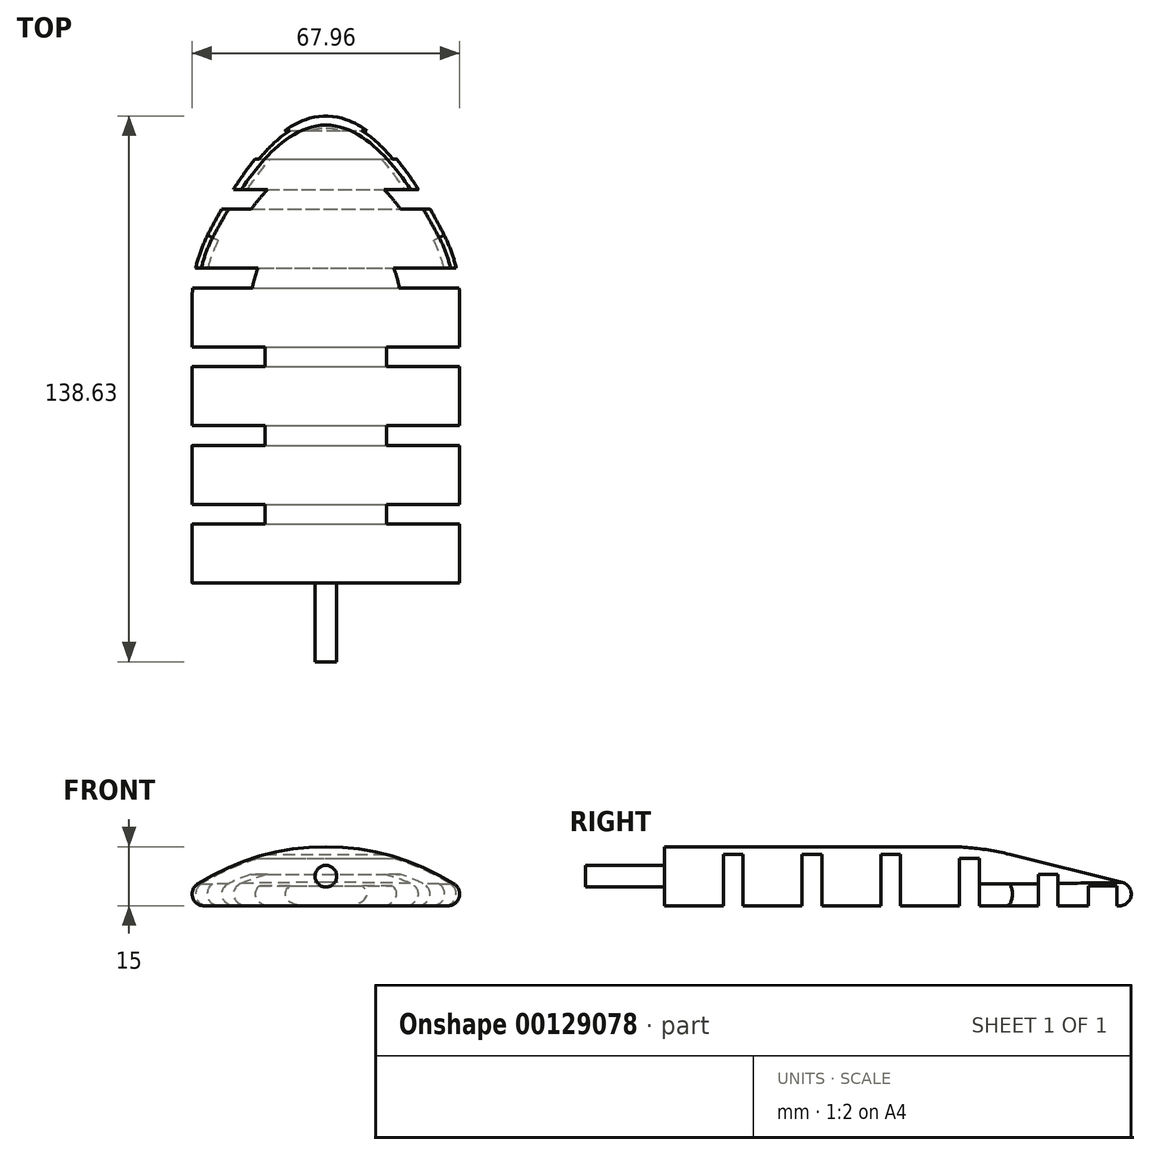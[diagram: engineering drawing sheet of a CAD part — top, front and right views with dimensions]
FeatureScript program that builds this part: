
annotation { "Feature Type Name" : "Feature", "Feature Type Description" : "" }
export const myFeature = defineFeature(function(context is Context, id is Id, definition is map)
    precondition{}
    {
        {
            var Q0;
            Q0=qCreatedBy(makeId("Front.planeOp"),FACE);
            var sketch = newSketch(context, id + "F0", { "sketchPlane" : qUnion([Q0])});
            skLineSegment(sketch, "E0", {"start": v(0, 0) * mm, "end": v(-40, 0) * mm});
            skLineSegment(sketch, "E1", {"start": v(0, 0) * mm, "end": v(40, 0) * mm});
            skArc(sketch, "E2", {"start": v(40, 0) * mm, "mid": v(0, 15) * mm, "end": v(-40, 0) * mm});
            skSolve(sketch);
        }
        {
            var Q0;
            Q0=makeQuery(id+"F0.imprint","IMPRINT",FACE,{"disambiguationData":[TD([[makeQuery(id+"F0.imprint","IMPRINT",EDGE,{"derivedFrom":sQuery(id+"F0.wireOp",EDGE,"E0")}),-1.0]])]});
            extrude(context, id + "F1", {"entities" : qUnion([Q0]), "endBound" : BoundingType.SYMMETRIC, "depth" : 100 * mm});
        }
        {
            var Q0;
            Q0=makeQuery(id+"F1.opExtrude","CAP_EDGE",EDGE,{"disambiguationData":[OSD([sQuery(id+"F0.wireOp",EDGE,"E2")])],"isStart":true});
            chamfer(context, id + "F2", {"entities" : qUnion([Q0]), "chamferType" : ChamferType.TWO_OFFSETS, "width1" : 60 * mm, "oppositeDirection" : false, "width2" : 15 * mm, "tangentPropagation" : true});
        }
        {
            var Q0;
            Q0=makeQuery(id+"F2.opChamfer","BLEND_EDGE",EDGE,{"disambiguationData":[OD(0.0)],"blendedFrom":[makeQuery(id+"F1.opExtrude","CAP_EDGE",EDGE,{"disambiguationData":[OSD([sQuery(id+"F0.wireOp",EDGE,"E2")])],"isStart":true}),makeQuery(id+"F1.opExtrude","SWEPT_FACE",FACE,{"disambiguationData":[OSD([sQuery(id+"F0.wireOp",EDGE,"E0"),sQuery(id+"F0.wireOp",EDGE,"E1")])]})],"blendedInto":[makeQuery(id+"F1.opExtrude","SWEPT_FACE",FACE,{"disambiguationData":[OSD([sQuery(id+"F0.wireOp",EDGE,"E0"),sQuery(id+"F0.wireOp",EDGE,"E1")])]})]});
            var Q1;
            Q1=makeQuery(id+"F2.opChamfer","BLEND_EDGE",EDGE,{"disambiguationData":[OD(1.0)],"blendedFrom":[makeQuery(id+"F1.opExtrude","CAP_EDGE",EDGE,{"disambiguationData":[OSD([sQuery(id+"F0.wireOp",EDGE,"E2")])],"isStart":true}),makeQuery(id+"F1.opExtrude","SWEPT_FACE",FACE,{"disambiguationData":[OSD([sQuery(id+"F0.wireOp",EDGE,"E0"),sQuery(id+"F0.wireOp",EDGE,"E1")])]})],"blendedInto":[makeQuery(id+"F1.opExtrude","SWEPT_FACE",FACE,{"disambiguationData":[OSD([sQuery(id+"F0.wireOp",EDGE,"E0"),sQuery(id+"F0.wireOp",EDGE,"E1")])]})]});
            var Q2;
            Q2=makeQuery(id+"F1.opExtrude","SWEPT_EDGE",EDGE,{"disambiguationData":[OSD([sQuery(id+"F0.wireOp",EDGE,"E0"),sQuery(id+"F0.wireOp",EDGE,"E2")])]});
            var Q3;
            Q3=makeQuery(id+"F1.opExtrude","SWEPT_EDGE",EDGE,{"disambiguationData":[OSD([sQuery(id+"F0.wireOp",EDGE,"E1"),sQuery(id+"F0.wireOp",EDGE,"E2")])]});
            fillet(context, id + "F3", {"entities" : qUnion([Q0, Q1, Q2, Q3]), "radius" : 3 * mm, "tangentPropagation" : true, "allowEdgeOverflow" : false});
        }
        {
            var Q0;
            Q0=makeQuery(id+"F1.opExtrude","CAP_FACE",FACE,{"disambiguationData":[OSD([sQuery(id+"F0.wireOp",EDGE,"E0"),sQuery(id+"F0.wireOp",EDGE,"E1"),sQuery(id+"F0.wireOp",EDGE,"E2")])],"isStart":false});
            extrude(context, id + "F4", {"entities" : qUnion([Q0]), "operationType" : NewBodyOperationType.ADD, "depth" : 40 * mm});
        }
        {
            var Q0;
            {var subQ0=sQuery(id+"F0.wireOp",EDGE,"E0");var subQ1=sQuery(id+"F0.wireOp",EDGE,"E2");Q0=makeQuery(id+"F3.opFillet","BLEND_EDGE",EDGE,{"blendedFrom":[makeQuery(id+"F1.opExtrude","SWEPT_EDGE",EDGE,{"disambiguationData":[OSD([subQ0,subQ1])]}),makeQuery(id+"F2.opChamfer","BLEND_EDGE",EDGE,{"disambiguationData":[OD(0.0)],"blendedFrom":[makeQuery(id+"F1.opExtrude","CAP_EDGE",EDGE,{"disambiguationData":[OSD([subQ1])],"isStart":true}),makeQuery(id+"F1.opExtrude","SWEPT_FACE",FACE,{"disambiguationData":[OSD([subQ0,sQuery(id+"F0.wireOp",EDGE,"E1")])]})],"blendedInto":[makeQuery(id+"F1.opExtrude","SWEPT_FACE",FACE,{"disambiguationData":[OSD([subQ0,sQuery(id+"F0.wireOp",EDGE,"E1")])]})]})],"blendedInto":[]});}
            fillet(context, id + "F5", {"entities" : qUnion([Q0]), "radius" : 65 * mm, "tangentPropagation" : true, "allowEdgeOverflow" : false});
        }
        {
            var Q0;
            Q0=makeQuery(id+"F4.opExtrude","CAP_FACE",FACE,{"disambiguationData":[OSD([sQuery(id+"F0.wireOp",EDGE,"E0"),sQuery(id+"F0.wireOp",EDGE,"E1"),sQuery(id+"F0.wireOp",EDGE,"E2")])],"isStart":false});
            var sketch = newSketch(context, id + "F6", { "sketchPlane" : qUnion([Q0])});
            skLineSegment(sketch, "E3", {"start": v(0, 0) * mm, "end": v(0, 15) * mm});
            skLineSegment(sketch, "E4", {"start": v(0, 7.5) * mm, "end": v(13.56, 7.5) * mm});
            skPoint(sketch, "E4.endSnap0", {"position": v(0, 7.5) * mm});
            skLineSegment(sketch, "E5", {"start": v(0, 7.5) * mm, "end": v(-13.5, 7.5) * mm});
            skCircle(sketch, "E6", {"center": v(0, 7.5) * mm, "radius": 2.75 * mm});
            skSolve(sketch);
        }
        {
            var Q0;
            {var subQ0=sQuery(id+"F6.wireOp",EDGE,"E4");var subQ3=sQuery(id+"F6.wireOp",EDGE,"E6");var subQ5=makeQuery(id+"F6.imprint","INTERSECT",VERTEX,{"derivedFrom":[subQ0,subQ3]});Q0=makeQuery(id+"F6.imprint","IMPRINT",FACE,{"disambiguationData":[TD([[makeQuery(id+"F6.imprint","IMPRINT",EDGE,{"disambiguationData":[TD([[subQ5,-1.0]])],"derivedFrom":subQ3}),1.0]])]});}
            var Q1;
            {var subQ0=sQuery(id+"F6.wireOp",EDGE,"E4");var subQ3=sQuery(id+"F6.wireOp",EDGE,"E6");var subQ5=makeQuery(id+"F6.imprint","INTERSECT",VERTEX,{"derivedFrom":[subQ0,subQ3]});Q1=makeQuery(id+"F6.imprint","IMPRINT",FACE,{"disambiguationData":[TD([[makeQuery(id+"F6.imprint","IMPRINT",EDGE,{"disambiguationData":[TD([[subQ5,1.0]])],"derivedFrom":subQ3}),1.0]])]});}
            var Q2;
            {var subQ0=sQuery(id+"F6.wireOp",EDGE,"E5");var subQ3=sQuery(id+"F6.wireOp",EDGE,"E6");var subQ5=makeQuery(id+"F6.imprint","INTERSECT",VERTEX,{"derivedFrom":[subQ0,subQ3]});Q2=makeQuery(id+"F6.imprint","IMPRINT",FACE,{"disambiguationData":[TD([[makeQuery(id+"F6.imprint","IMPRINT",EDGE,{"disambiguationData":[TD([[subQ5,-1.0]])],"derivedFrom":subQ3}),1.0]])]});}
            var Q3;
            {var subQ0=sQuery(id+"F6.wireOp",EDGE,"E5");var subQ3=sQuery(id+"F6.wireOp",EDGE,"E6");var subQ5=makeQuery(id+"F6.imprint","INTERSECT",VERTEX,{"derivedFrom":[subQ0,subQ3]});Q3=makeQuery(id+"F6.imprint","IMPRINT",FACE,{"disambiguationData":[TD([[makeQuery(id+"F6.imprint","IMPRINT",EDGE,{"disambiguationData":[TD([[subQ5,1.0]])],"derivedFrom":subQ3}),1.0]])]});}
            extrude(context, id + "F7", {"entities" : qUnion([Q0, Q1, Q2, Q3]), "operationType" : NewBodyOperationType.ADD, "depth" : 20 * mm});
        }
        {
            var Q0;
            {var subQ0=sQuery(id+"F0.wireOp",EDGE,"E1");var subQ1=sQuery(id+"F0.wireOp",EDGE,"E0");Q0=makeQuery(id+"F4.boolean.opBoolean","MERGE",FACE,{"derivedFrom":[makeQuery(id+"F1.opExtrude","SWEPT_FACE",FACE,{"disambiguationData":[OSD([subQ1,subQ0])]}),makeQuery(id+"F4.opExtrude","SWEPT_FACE",FACE,{"disambiguationData":[OSD([subQ1,subQ0])]})]});}
            var sketch = newSketch(context, id + "F8", { "sketchPlane" : qUnion([Q0])});
            skLineSegment(sketch, "E7", {"start": v(0, 90) * mm, "end": v(0, -25.63) * mm});
            skPoint(sketch, "E8", {"position": v(0, 75) * mm});
            skPoint(sketch, "E9", {"position": v(0, 70) * mm});
            skPoint(sketch, "E10", {"position": v(0, 55) * mm});
            skPoint(sketch, "E11", {"position": v(0, 50) * mm});
            skPoint(sketch, "E12", {"position": v(0, 35) * mm});
            skPoint(sketch, "E13", {"position": v(0, 30) * mm});
            skPoint(sketch, "E14", {"position": v(0, 15) * mm});
            skPoint(sketch, "E15", {"position": v(0, 10) * mm});
            skPoint(sketch, "E16", {"position": v(0, -5) * mm});
            skPoint(sketch, "E17", {"position": v(0, -10) * mm});
            skPoint(sketch, "E18", {"position": v(0, -25) * mm});
            skLineSegment(sketch, "E19", {"start": v(0, 70) * mm, "end": v(-30.98, 70) * mm});
            skLineSegment(sketch, "E20", {"start": v(0, 75) * mm, "end": v(30.98, 75) * mm});
            skLineSegment(sketch, "E21.bottom", {"start": v(-46.57, 70) * mm, "end": v(50.6, 70) * mm});
            skLineSegment(sketch, "E21.top", {"start": v(-46.57, 75) * mm, "end": v(50.6, 75) * mm});
            skLineSegment(sketch, "E21.left", {"start": v(-46.57, 70) * mm, "end": v(-46.57, 75) * mm});
            skLineSegment(sketch, "E21.right", {"start": v(50.6, 70) * mm, "end": v(50.6, 75) * mm});
            skLineSegment(sketch, "E22.bottom", {"start": v(-46.86, 50) * mm, "end": v(50.6, 50) * mm});
            skLineSegment(sketch, "E22.top", {"start": v(-46.86, 55) * mm, "end": v(50.6, 55) * mm});
            skLineSegment(sketch, "E22.left", {"start": v(-46.86, 50) * mm, "end": v(-46.86, 55) * mm});
            skLineSegment(sketch, "E22.right", {"start": v(50.6, 50) * mm, "end": v(50.6, 55) * mm});
            skLineSegment(sketch, "E23.bottom", {"start": v(-45.7, 30) * mm, "end": v(42.8, 30) * mm});
            skLineSegment(sketch, "E23.top", {"start": v(-45.7, 35) * mm, "end": v(42.8, 35) * mm});
            skLineSegment(sketch, "E23.left", {"start": v(-45.7, 30) * mm, "end": v(-45.7, 35) * mm});
            skLineSegment(sketch, "E23.right", {"start": v(42.8, 30) * mm, "end": v(42.8, 35) * mm});
            skLineSegment(sketch, "E24.bottom", {"start": v(-43.37, 15) * mm, "end": v(40.63, 15) * mm});
            skLineSegment(sketch, "E24.top", {"start": v(-43.37, 10) * mm, "end": v(40.63, 10) * mm});
            skLineSegment(sketch, "E24.left", {"start": v(-43.37, 15) * mm, "end": v(-43.37, 10) * mm});
            skLineSegment(sketch, "E24.right", {"start": v(40.63, 15) * mm, "end": v(40.63, 10) * mm});
            skLineSegment(sketch, "E25.bottom", {"start": v(-43.56, -5) * mm, "end": v(47.17, -5) * mm});
            skLineSegment(sketch, "E25.top", {"start": v(-43.56, -10) * mm, "end": v(47.17, -10) * mm});
            skLineSegment(sketch, "E25.left", {"start": v(-43.56, -5) * mm, "end": v(-43.56, -10) * mm});
            skLineSegment(sketch, "E25.right", {"start": v(47.17, -5) * mm, "end": v(47.17, -10) * mm});
            skLineSegment(sketch, "E26.bottom", {"start": v(-30.89, -25) * mm, "end": v(32.7, -25) * mm});
            skLineSegment(sketch, "E26.top", {"start": v(-30.89, -17.74) * mm, "end": v(32.7, -17.74) * mm});
            skLineSegment(sketch, "E26.left", {"start": v(-30.89, -25) * mm, "end": v(-30.89, -17.74) * mm});
            skLineSegment(sketch, "E26.right", {"start": v(32.7, -25) * mm, "end": v(32.7, -17.74) * mm});
            skSolve(sketch);
        }
        {
            var Q0;
            {var subQ0=sQuery(id+"F8.wireOp",EDGE,"E26.left");Q0=makeQuery(id+"F8.imprint","IMPRINT",FACE,{"disambiguationData":[TD([[makeQuery(id+"F8.imprint","IMPRINT",EDGE,{"derivedFrom":subQ0}),-1.0]])]});}
            var Q1;
            {var subQ0=sQuery(id+"F8.wireOp",EDGE,"E26.top");var subQ1=sQuery(id+"F8.wireOp",EDGE,"E7");var subQ2=makeQuery(id+"F8.imprint","INTERSECT",VERTEX,{"derivedFrom":[subQ1,subQ0]});Q1=makeQuery(id+"F8.imprint","IMPRINT",FACE,{"disambiguationData":[TD([[makeQuery(id+"F8.imprint","IMPRINT",EDGE,{"disambiguationData":[TD([[subQ2,-1.0]])],"derivedFrom":subQ1}),-1.0]])]});}
            var Q2;
            {var subQ0=sQuery(id+"F8.wireOp",EDGE,"E26.top");var subQ1=sQuery(id+"F8.wireOp",EDGE,"E7");var subQ2=makeQuery(id+"F8.imprint","INTERSECT",VERTEX,{"derivedFrom":[subQ1,subQ0]});Q2=makeQuery(id+"F8.imprint","IMPRINT",FACE,{"disambiguationData":[TD([[makeQuery(id+"F8.imprint","IMPRINT",EDGE,{"disambiguationData":[TD([[subQ2,-1.0]])],"derivedFrom":subQ1}),1.0]])]});}
            var Q3;
            {var subQ0=sQuery(id+"F8.wireOp",EDGE,"E26.right");Q3=makeQuery(id+"F8.imprint","IMPRINT",FACE,{"disambiguationData":[TD([[makeQuery(id+"F8.imprint","IMPRINT",EDGE,{"derivedFrom":subQ0}),1.0]])]});}
            var Q4;
            {var subQ0=sQuery(id+"F8.wireOp",EDGE,"E25.right");Q4=makeQuery(id+"F8.imprint","IMPRINT",FACE,{"disambiguationData":[TD([[makeQuery(id+"F8.imprint","IMPRINT",EDGE,{"derivedFrom":subQ0}),-1.0]])]});}
            var Q5;
            {var subQ0=sQuery(id+"F8.wireOp",EDGE,"E25.bottom");var subQ1=sQuery(id+"F8.wireOp",EDGE,"E7");var subQ2=makeQuery(id+"F8.imprint","INTERSECT",VERTEX,{"derivedFrom":[subQ1,subQ0]});Q5=makeQuery(id+"F8.imprint","IMPRINT",FACE,{"disambiguationData":[TD([[makeQuery(id+"F8.imprint","IMPRINT",EDGE,{"disambiguationData":[TD([[subQ2,-1.0]])],"derivedFrom":subQ1}),1.0]])]});}
            var Q6;
            {var subQ0=sQuery(id+"F8.wireOp",EDGE,"E25.bottom");var subQ1=sQuery(id+"F8.wireOp",EDGE,"E7");var subQ2=makeQuery(id+"F8.imprint","INTERSECT",VERTEX,{"derivedFrom":[subQ1,subQ0]});Q6=makeQuery(id+"F8.imprint","IMPRINT",FACE,{"disambiguationData":[TD([[makeQuery(id+"F8.imprint","IMPRINT",EDGE,{"disambiguationData":[TD([[subQ2,-1.0]])],"derivedFrom":subQ1}),-1.0]])]});}
            var Q7;
            {var subQ0=sQuery(id+"F8.wireOp",EDGE,"E25.left");Q7=makeQuery(id+"F8.imprint","IMPRINT",FACE,{"disambiguationData":[TD([[makeQuery(id+"F8.imprint","IMPRINT",EDGE,{"derivedFrom":subQ0}),1.0]])]});}
            var Q8;
            {var subQ0=sQuery(id+"F8.wireOp",EDGE,"E24.left");Q8=makeQuery(id+"F8.imprint","IMPRINT",FACE,{"disambiguationData":[TD([[makeQuery(id+"F8.imprint","IMPRINT",EDGE,{"derivedFrom":subQ0}),1.0]])]});}
            var Q9;
            {var subQ0=sQuery(id+"F8.wireOp",EDGE,"E24.bottom");var subQ1=sQuery(id+"F8.wireOp",EDGE,"E7");var subQ2=makeQuery(id+"F8.imprint","INTERSECT",VERTEX,{"derivedFrom":[subQ1,subQ0]});Q9=makeQuery(id+"F8.imprint","IMPRINT",FACE,{"disambiguationData":[TD([[makeQuery(id+"F8.imprint","IMPRINT",EDGE,{"disambiguationData":[TD([[subQ2,-1.0]])],"derivedFrom":subQ1}),-1.0]])]});}
            var Q10;
            {var subQ0=sQuery(id+"F8.wireOp",EDGE,"E24.bottom");var subQ1=sQuery(id+"F8.wireOp",EDGE,"E7");var subQ2=makeQuery(id+"F8.imprint","INTERSECT",VERTEX,{"derivedFrom":[subQ1,subQ0]});Q10=makeQuery(id+"F8.imprint","IMPRINT",FACE,{"disambiguationData":[TD([[makeQuery(id+"F8.imprint","IMPRINT",EDGE,{"disambiguationData":[TD([[subQ2,-1.0]])],"derivedFrom":subQ1}),1.0]])]});}
            var Q11;
            {var subQ0=sQuery(id+"F8.wireOp",EDGE,"E24.right");Q11=makeQuery(id+"F8.imprint","IMPRINT",FACE,{"disambiguationData":[TD([[makeQuery(id+"F8.imprint","IMPRINT",EDGE,{"derivedFrom":subQ0}),-1.0]])]});}
            var Q12;
            {var subQ0=sQuery(id+"F8.wireOp",EDGE,"E23.right");Q12=makeQuery(id+"F8.imprint","IMPRINT",FACE,{"disambiguationData":[TD([[makeQuery(id+"F8.imprint","IMPRINT",EDGE,{"derivedFrom":subQ0}),1.0]])]});}
            var Q13;
            {var subQ0=sQuery(id+"F8.wireOp",EDGE,"E23.top");var subQ1=sQuery(id+"F8.wireOp",EDGE,"E7");var subQ2=makeQuery(id+"F8.imprint","INTERSECT",VERTEX,{"derivedFrom":[subQ1,subQ0]});Q13=makeQuery(id+"F8.imprint","IMPRINT",FACE,{"disambiguationData":[TD([[makeQuery(id+"F8.imprint","IMPRINT",EDGE,{"disambiguationData":[TD([[subQ2,-1.0]])],"derivedFrom":subQ1}),1.0]])]});}
            var Q14;
            {var subQ0=sQuery(id+"F8.wireOp",EDGE,"E23.top");var subQ1=sQuery(id+"F8.wireOp",EDGE,"E7");var subQ2=makeQuery(id+"F8.imprint","INTERSECT",VERTEX,{"derivedFrom":[subQ1,subQ0]});Q14=makeQuery(id+"F8.imprint","IMPRINT",FACE,{"disambiguationData":[TD([[makeQuery(id+"F8.imprint","IMPRINT",EDGE,{"disambiguationData":[TD([[subQ2,-1.0]])],"derivedFrom":subQ1}),-1.0]])]});}
            var Q15;
            {var subQ0=sQuery(id+"F8.wireOp",EDGE,"E23.left");Q15=makeQuery(id+"F8.imprint","IMPRINT",FACE,{"disambiguationData":[TD([[makeQuery(id+"F8.imprint","IMPRINT",EDGE,{"derivedFrom":subQ0}),-1.0]])]});}
            var Q16;
            {var subQ0=sQuery(id+"F8.wireOp",EDGE,"E22.left");Q16=makeQuery(id+"F8.imprint","IMPRINT",FACE,{"disambiguationData":[TD([[makeQuery(id+"F8.imprint","IMPRINT",EDGE,{"derivedFrom":subQ0}),-1.0]])]});}
            var Q17;
            {var subQ0=sQuery(id+"F8.wireOp",EDGE,"E22.top");var subQ1=sQuery(id+"F8.wireOp",EDGE,"E7");var subQ2=makeQuery(id+"F8.imprint","INTERSECT",VERTEX,{"derivedFrom":[subQ1,subQ0]});Q17=makeQuery(id+"F8.imprint","IMPRINT",FACE,{"disambiguationData":[TD([[makeQuery(id+"F8.imprint","IMPRINT",EDGE,{"disambiguationData":[TD([[subQ2,-1.0]])],"derivedFrom":subQ1}),-1.0]])]});}
            var Q18;
            {var subQ0=sQuery(id+"F8.wireOp",EDGE,"E22.top");var subQ1=sQuery(id+"F8.wireOp",EDGE,"E7");var subQ2=makeQuery(id+"F8.imprint","INTERSECT",VERTEX,{"derivedFrom":[subQ1,subQ0]});Q18=makeQuery(id+"F8.imprint","IMPRINT",FACE,{"disambiguationData":[TD([[makeQuery(id+"F8.imprint","IMPRINT",EDGE,{"disambiguationData":[TD([[subQ2,-1.0]])],"derivedFrom":subQ1}),1.0]])]});}
            var Q19;
            {var subQ0=sQuery(id+"F8.wireOp",EDGE,"E22.right");Q19=makeQuery(id+"F8.imprint","IMPRINT",FACE,{"disambiguationData":[TD([[makeQuery(id+"F8.imprint","IMPRINT",EDGE,{"derivedFrom":subQ0}),1.0]])]});}
            var Q20;
            {var subQ0=sQuery(id+"F8.wireOp",EDGE,"E21.right");Q20=makeQuery(id+"F8.imprint","IMPRINT",FACE,{"disambiguationData":[TD([[makeQuery(id+"F8.imprint","IMPRINT",EDGE,{"derivedFrom":subQ0}),1.0]])]});}
            var Q21;
            {var subQ0=sQuery(id+"F8.wireOp",EDGE,"E21.top");var subQ1=sQuery(id+"F8.wireOp",EDGE,"E7");var subQ2=makeQuery(id+"F8.imprint","INTERSECT",VERTEX,{"derivedFrom":[subQ1,subQ0]});Q21=makeQuery(id+"F8.imprint","IMPRINT",FACE,{"disambiguationData":[TD([[makeQuery(id+"F8.imprint","IMPRINT",EDGE,{"disambiguationData":[TD([[subQ2,-1.0]])],"derivedFrom":subQ1}),1.0]])]});}
            var Q22;
            {var subQ0=sQuery(id+"F8.wireOp",EDGE,"E21.top");var subQ1=sQuery(id+"F8.wireOp",EDGE,"E7");var subQ2=makeQuery(id+"F8.imprint","INTERSECT",VERTEX,{"derivedFrom":[subQ1,subQ0]});Q22=makeQuery(id+"F8.imprint","IMPRINT",FACE,{"disambiguationData":[TD([[makeQuery(id+"F8.imprint","IMPRINT",EDGE,{"disambiguationData":[TD([[subQ2,-1.0]])],"derivedFrom":subQ1}),-1.0]])]});}
            var Q23;
            {var subQ0=sQuery(id+"F8.wireOp",EDGE,"E21.left");Q23=makeQuery(id+"F8.imprint","IMPRINT",FACE,{"disambiguationData":[TD([[makeQuery(id+"F8.imprint","IMPRINT",EDGE,{"derivedFrom":subQ0}),-1.0]])]});}
            extrude(context, id + "F9", {"entities" : qUnion([Q0, Q1, Q2, Q3, Q4, Q5, Q6, Q7, Q8, Q9, Q10, Q11, Q12, Q13, Q14, Q15, Q16, Q17, Q18, Q19, Q20, Q21, Q22, Q23]), "operationType" : NewBodyOperationType.REMOVE, "oppositeDirection" : true, "depth" : 5 * mm});
        }
        {
            var Q0;
            Q0=makeQuery(id+"F9.boolean.opBoolean","COPY",FACE,{"derivedFrom":makeQuery(id+"F9.opExtrude","CAP_FACE",FACE,{"disambiguationData":[OSD([sQuery(id+"F8.wireOp",EDGE,"E25.bottom"),sQuery(id+"F8.wireOp",EDGE,"E25.top"),sQuery(id+"F8.wireOp",EDGE,"E25.left"),sQuery(id+"F8.wireOp",EDGE,"E25.right")])],"isStart":false})});
            extrude(context, id + "F10", {"entities" : qUnion([Q0]), "operationType" : NewBodyOperationType.REMOVE, "oppositeDirection" : true, "depth" : 3 * mm});
        }
        {
            var Q0;
            Q0=makeQuery(id+"F9.boolean.opBoolean","COPY",FACE,{"derivedFrom":makeQuery(id+"F9.opExtrude","CAP_FACE",FACE,{"disambiguationData":[OSD([sQuery(id+"F8.wireOp",EDGE,"E24.bottom"),sQuery(id+"F8.wireOp",EDGE,"E24.top"),sQuery(id+"F8.wireOp",EDGE,"E24.left"),sQuery(id+"F8.wireOp",EDGE,"E24.right")])],"isStart":false})});
            extrude(context, id + "F11", {"entities" : qUnion([Q0]), "operationType" : NewBodyOperationType.REMOVE, "oppositeDirection" : true, "depth" : 7 * mm});
        }
        {
            var Q0;
            Q0=makeQuery(id+"F9.boolean.opBoolean","COPY",FACE,{"derivedFrom":makeQuery(id+"F9.opExtrude","CAP_FACE",FACE,{"disambiguationData":[OSD([sQuery(id+"F8.wireOp",EDGE,"E23.bottom"),sQuery(id+"F8.wireOp",EDGE,"E23.top"),sQuery(id+"F8.wireOp",EDGE,"E23.left"),sQuery(id+"F8.wireOp",EDGE,"E23.right")])],"isStart":false})});
            var Q1;
            Q1=makeQuery(id+"F9.boolean.opBoolean","COPY",FACE,{"derivedFrom":makeQuery(id+"F9.opExtrude","CAP_FACE",FACE,{"disambiguationData":[OSD([sQuery(id+"F8.wireOp",EDGE,"E22.bottom"),sQuery(id+"F8.wireOp",EDGE,"E22.top"),sQuery(id+"F8.wireOp",EDGE,"E22.left"),sQuery(id+"F8.wireOp",EDGE,"E22.right")])],"isStart":false})});
            var Q2;
            Q2=makeQuery(id+"F9.boolean.opBoolean","COPY",FACE,{"derivedFrom":makeQuery(id+"F9.opExtrude","CAP_FACE",FACE,{"disambiguationData":[OSD([sQuery(id+"F8.wireOp",EDGE,"E21.bottom"),sQuery(id+"F8.wireOp",EDGE,"E21.top"),sQuery(id+"F8.wireOp",EDGE,"E21.left"),sQuery(id+"F8.wireOp",EDGE,"E21.right")])],"isStart":false})});
            extrude(context, id + "F12", {"entities" : qUnion([Q0, Q1, Q2]), "operationType" : NewBodyOperationType.REMOVE, "oppositeDirection" : true, "depth" : 8 * mm});
        }
    });
